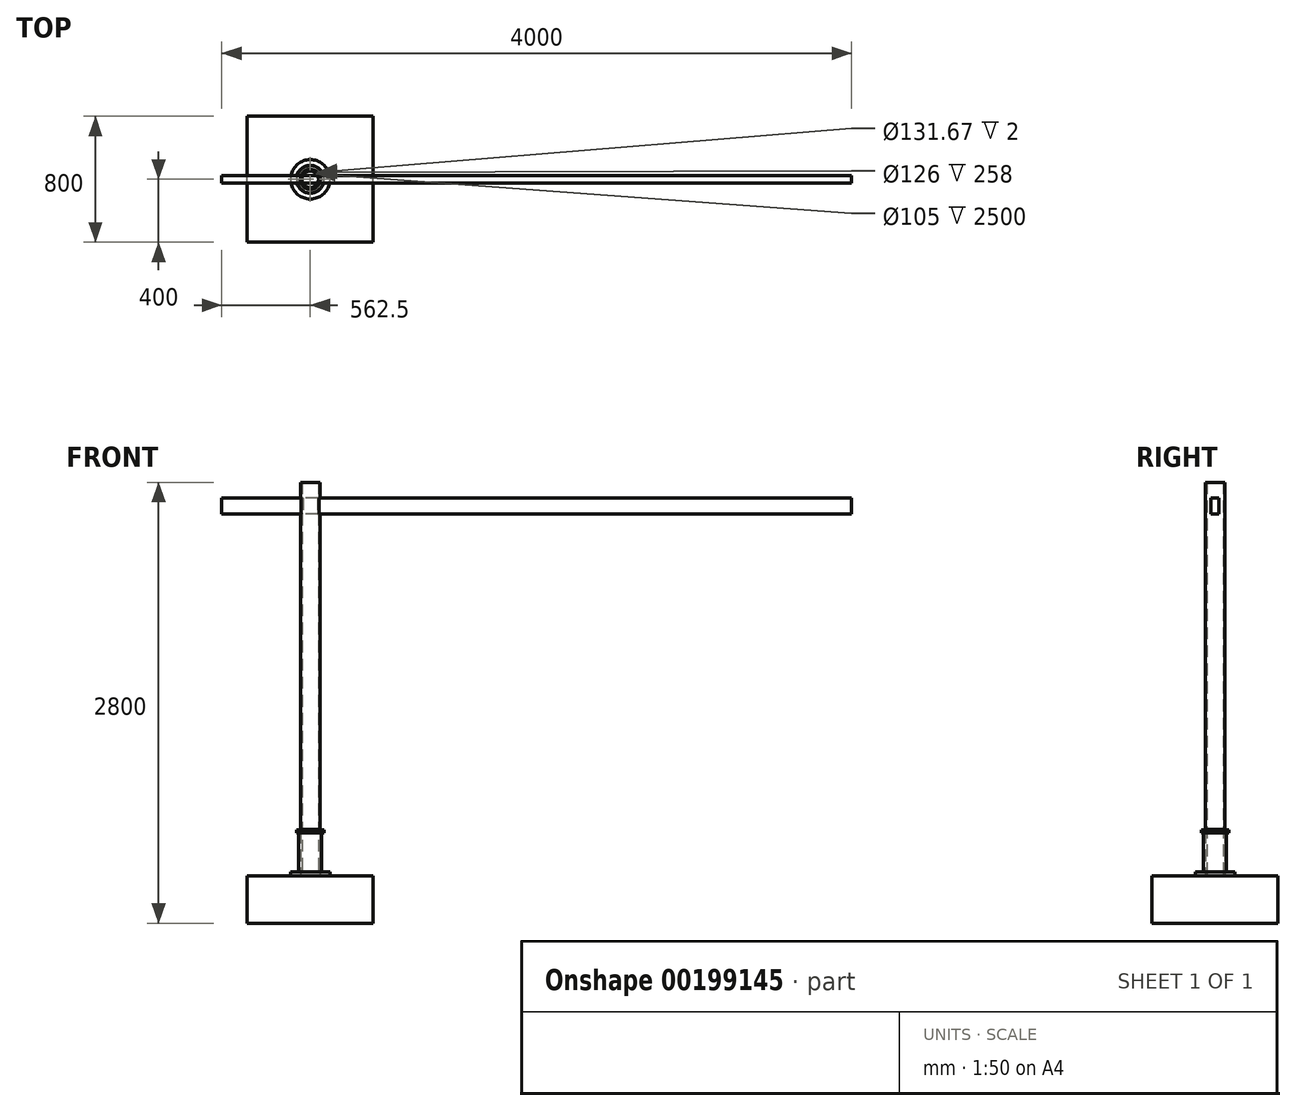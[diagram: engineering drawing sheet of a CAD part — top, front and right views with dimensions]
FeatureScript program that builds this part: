
annotation { "Feature Type Name" : "Feature", "Feature Type Description" : "" }
export const myFeature = defineFeature(function(context is Context, id is Id, definition is map)
    precondition{}
    {
        {
            var Q0;
            Q0=qCreatedBy(makeId("Top.planeOp"),FACE);
            var sketch = newSketch(context, id + "F0", { "sketchPlane" : qUnion([Q0])});
            skCircle(sketch, "E0", {"center": v(0, 0) * mm, "radius": 62.5 * mm});
            skCircle(sketch, "E1.0", {"center": v(0, 0) * mm, "radius": 52.5 * mm});
            skSolve(sketch);
        }
        {
            var Q0;
            Q0 = qSketchRegion(id + "F0", true);
            extrude(context, id + "F1", {"entities" : qUnion([Q0]), "depth" : 2500 * mm});
        }
        {
            var Q0;
            Q0=qCreatedBy(makeId("Right.planeOp"),FACE);
            cPlane(context, id + "F2", {"entities" : qUnion([Q0]), "cplaneType" : CPlaneType.OFFSET, "offset" : 62.5 * mm, "oppositeDirection" : true, "width" : 150 * mm, "height" : 150 * mm});
        }
        {
            var Q0;
            Q0=qCreatedBy(id+"F2.planeOp",FACE);
            var sketch = newSketch(context, id + "F3", { "sketchPlane" : qUnion([Q0])});
            skLineSegment(sketch, "E2", {"start": v(0, 0) * mm, "end": v(0, 2125.84) * mm, "construction": true});
            skLineSegment(sketch, "E3.bottom", {"start": v(25, 2300) * mm, "end": v(-25, 2300) * mm});
            skLineSegment(sketch, "E3.top", {"start": v(25, 2400) * mm, "end": v(-25, 2400) * mm});
            skLineSegment(sketch, "E3.left", {"start": v(25, 2300) * mm, "end": v(25, 2400) * mm});
            skLineSegment(sketch, "E3.right", {"start": v(-25, 2300) * mm, "end": v(-25, 2400) * mm});
            skSolve(sketch);
        }
        {
            var Q0;
            Q0 = qSketchRegion(id + "F3", true);
            extrude(context, id + "F4", {"entities" : qUnion([Q0]), "operationType" : NewBodyOperationType.REMOVE, "endBound" : BoundingType.THROUGH_ALL, "depth" : 25 * mm});
        }
        {
            var Q0;
            Q0=qCreatedBy(id+"F2.planeOp",FACE);
            var sketch = newSketch(context, id + "F5", { "sketchPlane" : qUnion([Q0])});
            skLineSegment(sketch, "E4.bottom", {"start": v(25, 2400) * mm, "end": v(-25, 2400) * mm});
            skLineSegment(sketch, "E4.top", {"start": v(25, 2300) * mm, "end": v(-25, 2300) * mm});
            skLineSegment(sketch, "E4.left", {"start": v(25, 2400) * mm, "end": v(25, 2300) * mm});
            skLineSegment(sketch, "E4.right", {"start": v(-25, 2400) * mm, "end": v(-25, 2300) * mm});
            skSolve(sketch);
        }
        {
            var Q0;
            Q0 = qSketchRegion(id + "F5", true);
            extrude(context, id + "F6", {"entities" : qUnion([Q0]), "operationType" : NewBodyOperationType.ADD, "depth" : 3500 * mm, "hasSecondDirection" : true, "secondDirectionOppositeDirection" : true, "secondDirectionDepth" : 500 * mm});
        }
        {
            var Q0;
            Q0=qCreatedBy(makeId("Top.planeOp"),FACE);
            var sketch = newSketch(context, id + "F7", { "sketchPlane" : qUnion([Q0])});
            skLineSegment(sketch, "E5.bottom", {"start": v(-400, -400) * mm, "end": v(400, -400) * mm});
            skLineSegment(sketch, "E5.top", {"start": v(-400, 400) * mm, "end": v(400, 400) * mm});
            skLineSegment(sketch, "E5.left", {"start": v(-400, -400) * mm, "end": v(-400, 400) * mm});
            skLineSegment(sketch, "E5.right", {"start": v(400, -400) * mm, "end": v(400, 400) * mm});
            skPoint(sketch, "E5.middle", {"position": v(0, 0) * mm});
            skSolve(sketch);
        }
        {
            var Q0;
            Q0 = qSketchRegion(id + "F7", true);
            extrude(context, id + "F8", {"entities" : qUnion([Q0]), "oppositeDirection" : true, "depth" : 300 * mm});
        }
        {
            var Q0;
            Q0=qCreatedBy(makeId("Top.planeOp"),FACE);
            var sketch = newSketch(context, id + "F9", { "sketchPlane" : qUnion([Q0])});
            skCircle(sketch, "E6", {"center": v(0, 0) * mm, "radius": 125 * mm});
            skSolve(sketch);
        }
        {
            var Q0;
            Q0 = qSketchRegion(id + "F9", true);
            extrude(context, id + "F10", {"entities" : qUnion([Q0]), "depth" : 25 * mm});
        }
        {
            var Q0;
            Q0=makeQuery(id+"F10.opExtrude","CAP_FACE",FACE,{"disambiguationData":[OSD([sQuery(id+"F9.wireOp",EDGE,"E6")])],"isStart":false});
            var sketch = newSketch(context, id + "F11", { "sketchPlane" : qUnion([Q0])});
            skCircle(sketch, "E7", {"center": v(0, 0) * mm, "radius": 63 * mm});
            skCircle(sketch, "E8.0", {"center": v(0, 0) * mm, "radius": 73 * mm});
            skSolve(sketch);
        }
        {
            var Q0;
            Q0 = qSketchRegion(id + "F11", true);
            extrude(context, id + "F12", {"entities" : qUnion([Q0]), "operationType" : NewBodyOperationType.ADD, "depth" : 250 * mm});
        }
        {
            var Q0;
            Q0=makeQuery(id+"F12.opExtrude","CAP_FACE",FACE,{"disambiguationData":[OSD([sQuery(id+"F11.wireOp",EDGE,"E7"),sQuery(id+"F11.wireOp",EDGE,"E8.0")])],"isStart":false});
            var sketch = newSketch(context, id + "F13", { "sketchPlane" : qUnion([Q0])});
            skCircle(sketch, "E9", {"center": v(0, 0) * mm, "radius": 63 * mm});
            skCircle(sketch, "E10.0", {"center": v(0, 0) * mm, "radius": 88 * mm});
            skSolve(sketch);
        }
        {
            var Q0;
            Q0 = qSketchRegion(id + "F13", true);
            extrude(context, id + "F14", {"entities" : qUnion([Q0]), "operationType" : NewBodyOperationType.ADD, "depth" : 10 * mm});
        }
        {
            var Q0;
            Q0=makeQuery(id+"F14.opExtrude","CAP_FACE",FACE,{"disambiguationData":[OSD([sQuery(id+"F13.wireOp",EDGE,"E9"),sQuery(id+"F13.wireOp",EDGE,"E10.0")])],"isStart":false});
            var sketch = newSketch(context, id + "F15", { "sketchPlane" : qUnion([Q0])});
            skCircle(sketch, "E11", {"center": v(0, 0) * mm, "radius": 57.5 * mm});
            skCircle(sketch, "E12", {"center": v(0, 0) * mm, "radius": 65.83 * mm});
            skSolve(sketch);
        }
        {
            var Q0;
            Q0 = qSketchRegion(id + "F15", true);
            extrude(context, id + "F16", {"entities" : qUnion([Q0]), "operationType" : NewBodyOperationType.REMOVE, "depth" : 10 * mm, "hasSecondDirection" : true, "secondDirectionOppositeDirection" : true, "secondDirectionDepth" : 2 * mm});
        }
        {
            var Q0;
            Q0=makeQuery(id+"F14.opExtrude","CAP_FACE",FACE,{"disambiguationData":[OSD([sQuery(id+"F13.wireOp",EDGE,"E9"),sQuery(id+"F13.wireOp",EDGE,"E10.0")])],"isStart":false});
            var sketch = newSketch(context, id + "F17", { "sketchPlane" : qUnion([Q0])});
            skArc(sketch, "E13", {"start": v(58.66, -1.42) * mm, "mid": v(1.42, 58.66) * mm, "end": v(-58.66, 1.42) * mm});
            skArc(sketch, "E14", {"start": v(87.44, -2.12) * mm, "mid": v(2.12, 87.44) * mm, "end": v(-87.44, 2.12) * mm});
            skLineSegment(sketch, "E15", {"start": v(-87.44, 2.12) * mm, "end": v(-58.66, 1.42) * mm});
            skLineSegment(sketch, "E16.trimOffspring", {"start": v(58.66, -1.42) * mm, "end": v(87.44, -2.12) * mm});
            skSolve(sketch);
        }
        {
            var Q0;
            Q0 = qSketchRegion(id + "F17", true);
            extrude(context, id + "F18", {"entities" : qUnion([Q0]), "depth" : 8 * mm});
        }
        {
            var Q0;
            Q0=makeQuery(id+"F18.opExtrude","SWEPT_BODY",BODY,{"disambiguationData":[OSD([sQuery(id+"F17.wireOp",EDGE,"E13"),sQuery(id+"F17.wireOp",EDGE,"E14"),sQuery(id+"F17.wireOp",EDGE,"E15"),sQuery(id+"F17.wireOp",EDGE,"E16.trimOffspring")])]});
            var Q1;
            Q1=makeQuery(id+"F18.opExtrude","SWEPT_FACE",FACE,{"disambiguationData":[OSD([sQuery(id+"F17.wireOp",EDGE,"E15")])]});
            mirror(context, id + "F19", {"entities" : qUnion([Q0]), "mirrorPlane" : qUnion([Q1])});
        }
    });
